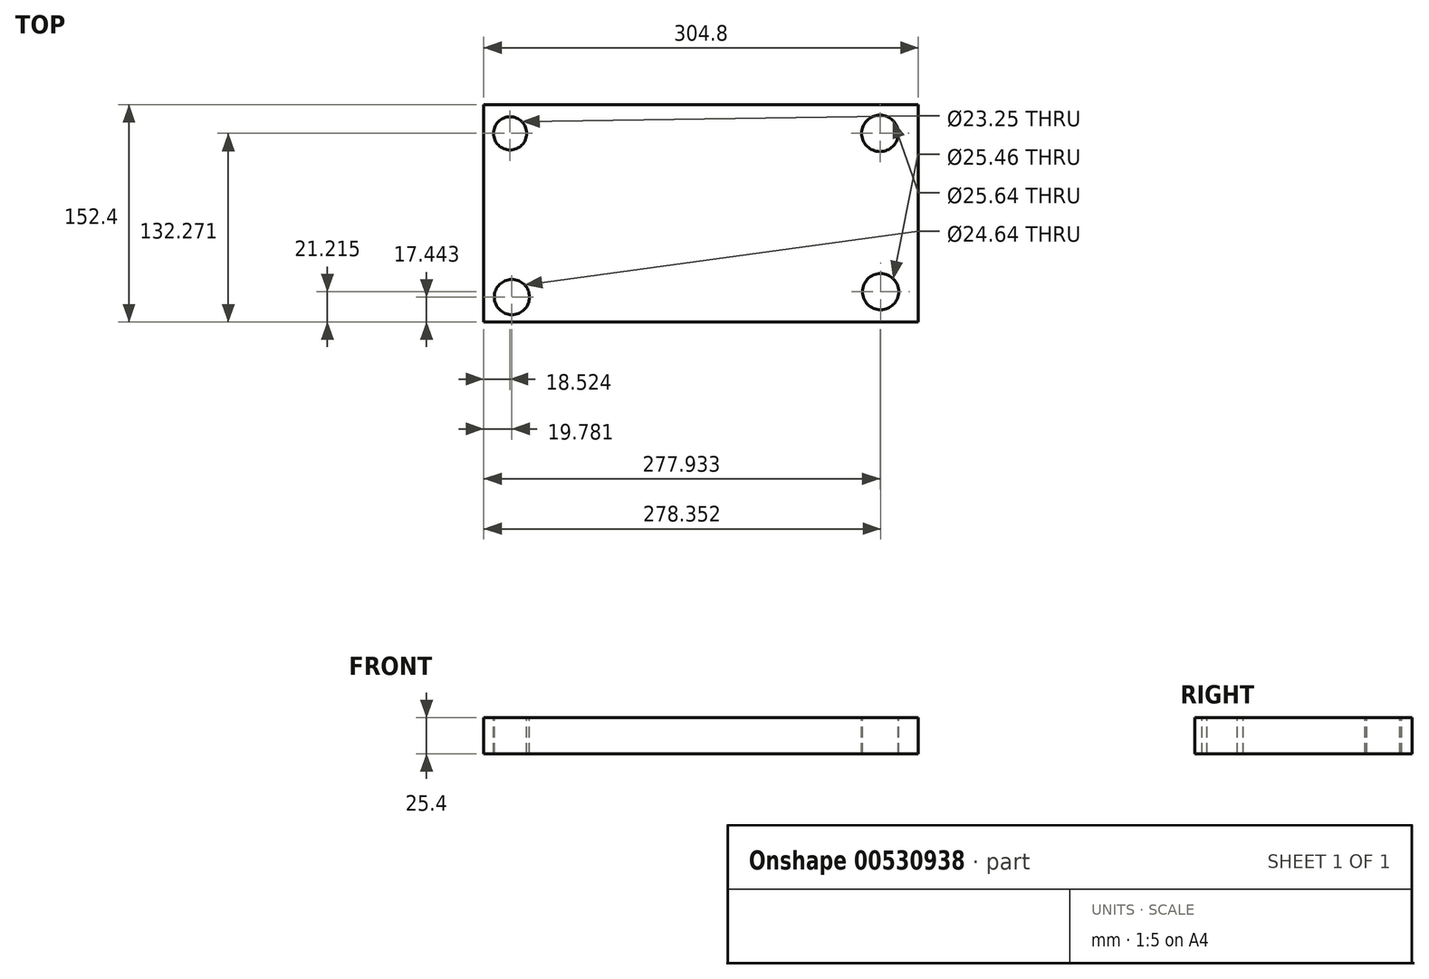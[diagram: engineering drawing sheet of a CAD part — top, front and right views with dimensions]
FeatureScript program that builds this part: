
annotation { "Feature Type Name" : "Feature", "Feature Type Description" : "" }
export const myFeature = defineFeature(function(context is Context, id is Id, definition is map)
    precondition{}
    {
        {
            var Q0;
            Q0=qCreatedBy(makeId("Top.planeOp"),FACE);
            var sketch = newSketch(context, id + "F0", { "sketchPlane" : qUnion([Q0])});
            skLineSegment(sketch, "E0.bottom", {"start": v(152.4, 76.2) * mm, "end": v(-152.4, 76.2) * mm});
            skLineSegment(sketch, "E0.top", {"start": v(152.4, -76.2) * mm, "end": v(-152.4, -76.2) * mm});
            skLineSegment(sketch, "E0.left", {"start": v(152.4, 76.2) * mm, "end": v(152.4, -76.2) * mm});
            skLineSegment(sketch, "E0.right", {"start": v(-152.4, 76.2) * mm, "end": v(-152.4, -76.2) * mm});
            skPoint(sketch, "E0.middle", {"position": v(0, 0) * mm});
            skSolve(sketch);
        }
        {
            var Q0;
            Q0=makeQuery(id+"F0.imprint","IMPRINT",FACE,{"disambiguationData":[TD([[makeQuery(id+"F0.imprint","IMPRINT",EDGE,{"derivedFrom":sQuery(id+"F0.wireOp",EDGE,"E0.bottom")}),1.0]])]});
            extrude(context, id + "F1", {"entities" : qUnion([Q0]), "endBound" : BoundingType.SYMMETRIC, "depth" : 25.4 * mm, "offsetDistance" : 25.4 * mm});
        }
        {
            var Q0;
            Q0=qCreatedBy(makeId("Top.planeOp"),FACE);
            var sketch = newSketch(context, id + "F2", { "sketchPlane" : qUnion([Q0])});
            skCircle(sketch, "E1", {"center": v(-133.88, 56.07) * mm, "radius": 11.62 * mm});
            skCircle(sketch, "E2", {"center": v(-132.62, -58.76) * mm, "radius": 12.32 * mm});
            skCircle(sketch, "E3", {"center": v(125.53, 56.07) * mm, "radius": 12.82 * mm});
            skCircle(sketch, "E4", {"center": v(125.95, -54.98) * mm, "radius": 12.73 * mm});
            skSolve(sketch);
        }
        {
            var Q0;
            Q0 = qSketchRegion(id + "F2", true);
            extrude(context, id + "F3", {"entities" : qUnion([Q0]), "operationType" : NewBodyOperationType.REMOVE, "endBound" : BoundingType.SYMMETRIC, "oppositeDirection" : true, "depth" : 25.4 * mm, "offsetDistance" : 25.4 * mm});
        }
    });
